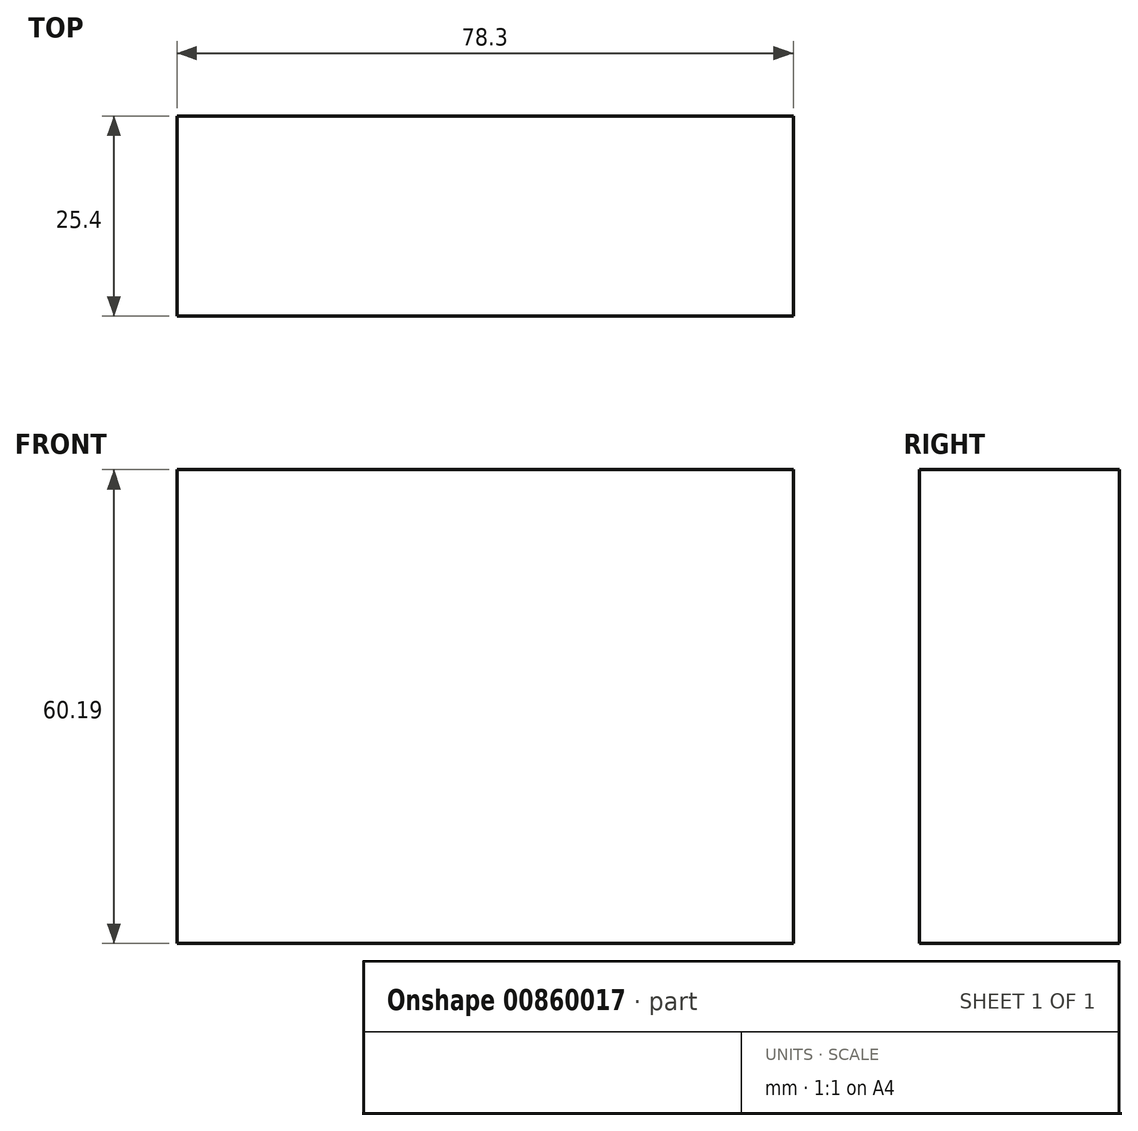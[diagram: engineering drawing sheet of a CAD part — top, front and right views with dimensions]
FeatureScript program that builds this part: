
annotation { "Feature Type Name" : "Feature", "Feature Type Description" : "" }
export const myFeature = defineFeature(function(context is Context, id is Id, definition is map)
    precondition{}
    {
        {
            var Q0;
            Q0=qCreatedBy(makeId("Front.planeOp"),FACE);
            var sketch = newSketch(context, id + "F0", { "sketchPlane" : qUnion([Q0])});
            skLineSegment(sketch, "E0.bottom", {"start": v(-72.68, 39.52) * mm, "end": v(5.62, 39.52) * mm});
            skLineSegment(sketch, "E0.top", {"start": v(-72.68, -20.67) * mm, "end": v(5.62, -20.67) * mm});
            skLineSegment(sketch, "E0.left", {"start": v(-72.68, 39.52) * mm, "end": v(-72.68, -20.67) * mm});
            skLineSegment(sketch, "E0.right", {"start": v(5.62, 39.52) * mm, "end": v(5.62, -20.67) * mm});
            skSolve(sketch);
        }
        {
            var Q0;
            Q0=makeQuery(id+"F0.imprint","IMPRINT",FACE,{"disambiguationData":[TD([[makeQuery(id+"F0.imprint","IMPRINT",EDGE,{"derivedFrom":sQuery(id+"F0.wireOp",EDGE,"E0.bottom")}),-1.0]])]});
            extrude(context, id + "F1", {"entities" : qUnion([Q0]), "depth" : 25.4 * mm, "offsetDistance" : 25.4 * mm});
        }
    });
